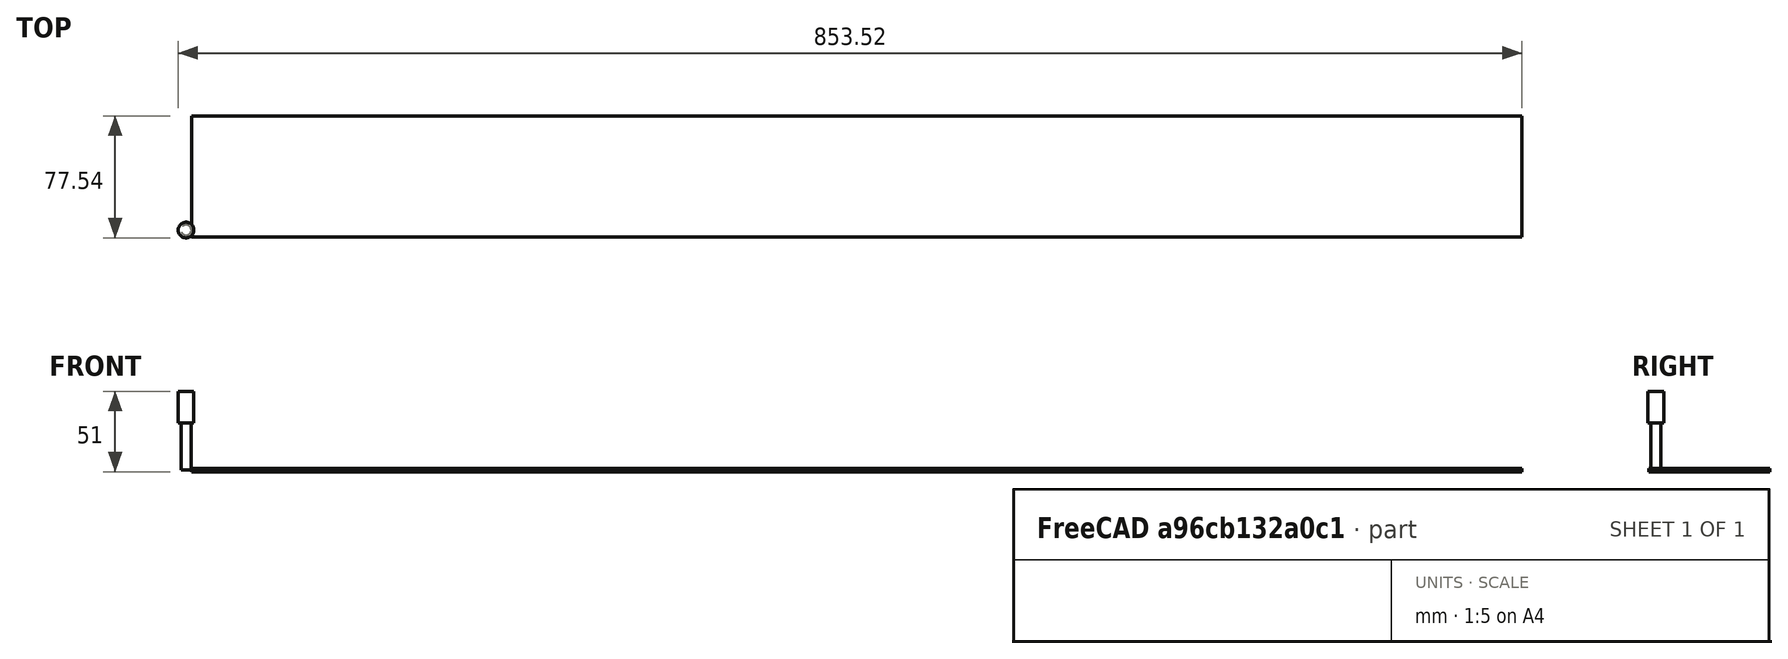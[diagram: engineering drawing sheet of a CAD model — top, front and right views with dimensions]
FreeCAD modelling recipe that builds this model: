
FCSTD DOCUMENT  (FreeCAD 0.19R14555 (Git shallow))
Label: MSSign
License: All rights reserved
LicenseURL: http://en.wikipedia.org/wiki/All_rights_reserved
objects: Path::FeaturePython×3, Part::Part2DObjectPython×2, App::DocumentObjectGroup×2, Part::FeaturePython×2, Sketcher::SketchObject×1, PartDesign::Body×1, App::FeaturePython×1, Path::FeatureCompoundPython×1, Mesh::FeaturePython×1, App::MeasureDistance×1
note: 6 computed .brp shape members not serialized (recipe doc carries the construction recipe); baked Part::Feature solids carry a one-line shape summary decoded from their .brp

FEATURE [Sketcher::SketchObject] Sketch
  FullyConstrained = true
  MapMode = 5
  Support = -> [XY_Plane]
FEATURE [PartDesign::Body] Body
  Group = -> [Sketch]
  Origin = -> Origin
FEATURE [Part::Part2DObjectPython] ShapeString  # Draft 2D object (typed FeaturePython)
  FontFile = <userpath>/Documents/MensShed/FreeCAD/CamBam Stick Fonts/1CamBam_Stick_5.ttf
  Size = 32
  String = The Men's Shed
  Tracking = 0
FEATURE [App::FeaturePython] SetupSheet  # Path/CAM operation (typed FeaturePython)
  ClearanceHeightExpression = OpStockZMax+SetupSheet.ClearanceHeightOffset
  ClearanceHeightOffset = 5
  CoolantMode = 0
  CoolantModes = None | Flood | Mist
  FinalDepthExpression = OpFinalDepth
  HorizRapid = 0
  SafeHeightExpression = OpStockZMax+SetupSheet.SafeHeightOffset
  SafeHeightOffset = 3
  StartDepthExpression = OpStartDepth
  StepDownExpression = OpToolDiameter
  VertRapid = 0
FEATURE [Part::Part2DObjectPython] Clone2D  label="Model-ShapeString"  # Draft 2D object (typed FeaturePython)
  Fuse = false
  Objects = -> [ShapeString]
  PathResource = Model
  Scale = (1,1,1)
FEATURE [App::DocumentObjectGroup] Model
  Group = -> [Clone2D]
FEATURE [Part::FeaturePython] Stock  # WARN: FeaturePython — macro-defined, semantics opaque (R4)
  Base = -> Model
  ExtXneg = 1
  ExtXpos = 1
  ExtYneg = 1
  ExtYpos = 1
  ExtZneg = 1
  ExtZpos = 1
  Placement = pos=(4.56881,-3.52294,0) rot=(0,0,1;0rad)
  StockType = FromBase
FEATURE [Part::FeaturePython] ToolBit001  label="6.4mm Endmill"  # Path/CAM toolbit (typed FeaturePython)
  BitPropertyNames = Chipload | CuttingEdgeHeight | Diameter | Flutes | Length | Material | ShankDiameter
  BitShape = /app/freecad/Mod/Path/Tools/Shape/endmill.fcstd
  Chipload = 0
  CuttingEdgeHeight = 30
  Diameter = 6.4
  File = <userpath>/Documents/MensShed/FreeCAD/Bit/6.4mm_Endmill.fctb
  Flutes = 0
  Length = 50
  Material = 0
  ShankDiameter = 10
  ShapeName = endmill
FEATURE [Path::FeaturePython] __4mm_Endmill  label="6.4mm Endmill001"  # Path/CAM operation (typed FeaturePython)
  HorizFeed = 10
  HorizRapid = 0
  SpindleDir = 0
  SpindleSpeed = 10000
  Tool = -> ToolBit001
  ToolNumber = 1
  VertFeed = 10
  VertRapid = 0
  expr: HorizRapid = SetupSheet.HorizRapid
  expr: VertRapid = SetupSheet.VertRapid
FEATURE [App::DocumentObjectGroup] Tools
  Group = -> [__4mm_Endmill]
FEATURE [Path::FeaturePython] Engrave  # Path/CAM operation (typed FeaturePython)
  Active = true
  ClearanceHeight = 6
  CoolantMode = None
  CycleTime = 00:06:48
  FinalDepth = -2
  OpFinalDepth = -1
  OpStartDepth = 0
  OpStockZMax = 1
  OpStockZMin = -1
  OpToolDiameter = 6.4
  SafeHeight = 4
  StartDepth = 0
  StartVertex = 0
  StepDown = 1
  ToolController = -> __4mm_Endmill
  expr: ClearanceHeight = OpStockZMax + SetupSheet.ClearanceHeightOffset
  expr: SafeHeight = OpStockZMax + SetupSheet.SafeHeightOffset
  expr: StepDown = 1
  expr: FinalDepth = -2
  expr: StartDepth = OpStartDepth
FEATURE [Path::FeatureCompoundPython] Operations  # Path/CAM operation (typed FeaturePython)
  Group = -> [Engrave]
  UsePlacements = false
FEATURE [Path::FeaturePython] Job  # Path/CAM operation (typed FeaturePython)
  CycleTime = 00:06:48
  Fixtures = G54
  GeometryTolerance = 0.01
  LastPostProcessDate = 2021-12-07 09:21:36.872545
  LastPostProcessOutput = <userpath>/Documents/MensShed/MSSign.ngc
  Model = -> Model
  Operations = -> Operations
  OrderOutputBy = 0
  PostProcessor = 7
  PostProcessorOutputFile = <userpath>/Documents/MensShed/MSSign.ngc
  SetupSheet = -> SetupSheet
  SplitOutput = false
  Stock = -> Stock
  Tools = -> Tools
FEATURE [Mesh::FeaturePython] CutMaterial  # WARN: FeaturePython — macro-defined, semantics opaque (R4)
FEATURE [App::MeasureDistance] Distance  label="Distance: 387.16 mm"
  Distance = 387.159
  P1 = (5.32569,-0.880734,6)
  P2 = (392.356,5.10442,-2)
